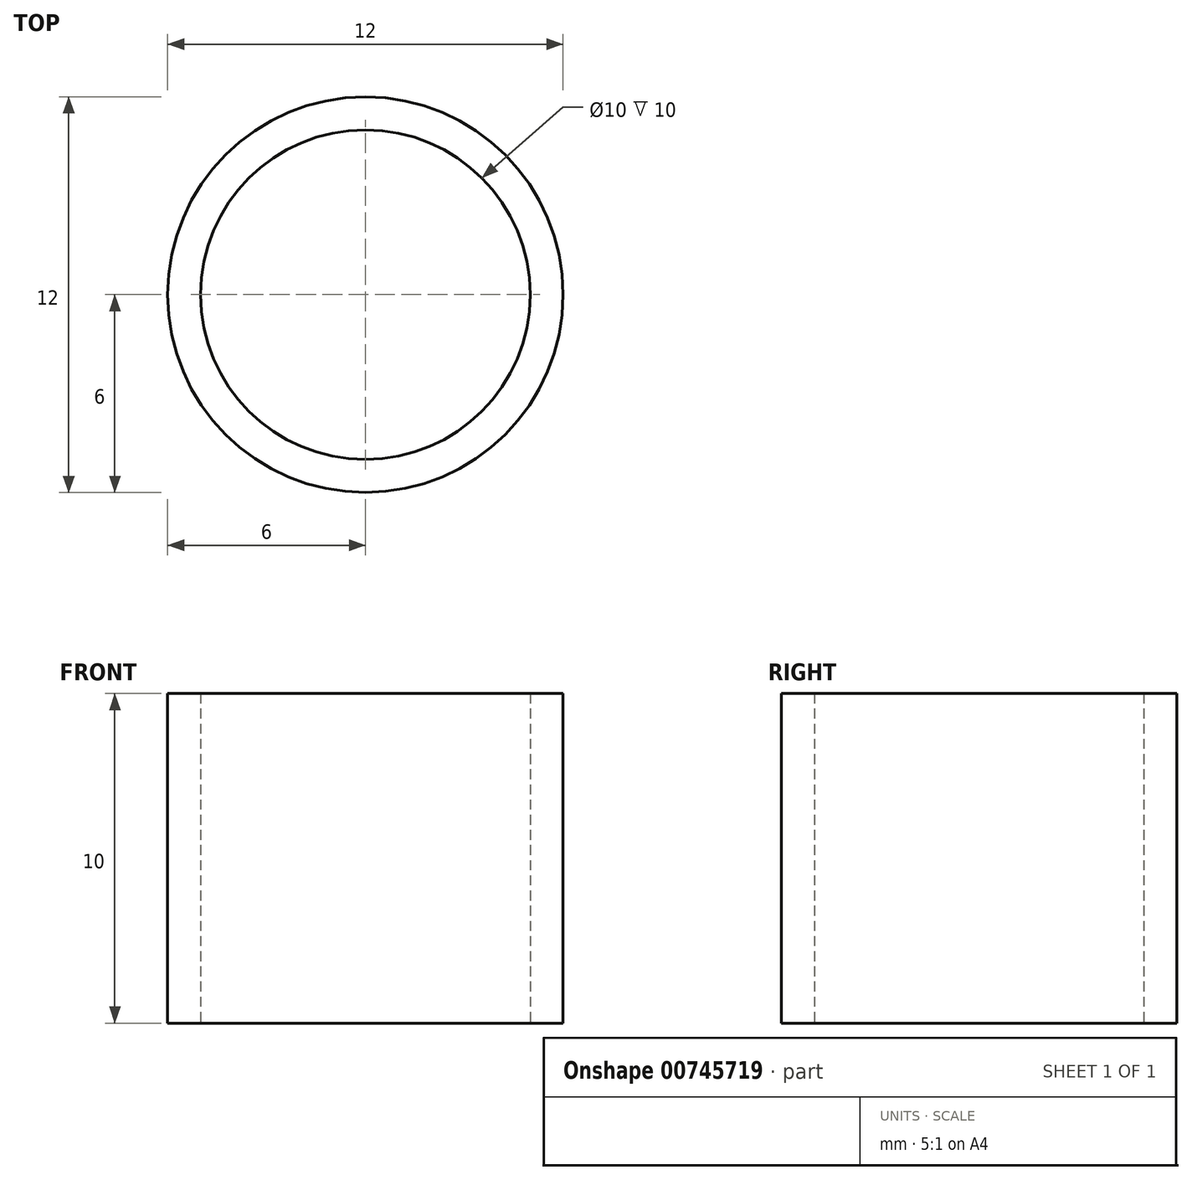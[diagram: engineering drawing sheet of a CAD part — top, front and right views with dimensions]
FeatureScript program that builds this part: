
annotation { "Feature Type Name" : "Feature", "Feature Type Description" : "" }
export const myFeature = defineFeature(function(context is Context, id is Id, definition is map)
    precondition{}
    {
        {
            var Q0;
            Q0=qCreatedBy(makeId("Top.planeOp"),FACE);
            var sketch = newSketch(context, id + "F0", { "sketchPlane" : qUnion([Q0])});
            skCircle(sketch, "E0", {"center": v(0, 0) * mm, "radius": 5 * mm});
            skCircle(sketch, "E1", {"center": v(0, 0) * mm, "radius": 6 * mm});
            skSolve(sketch);
        }
        {
            var Q0;
            Q0=makeQuery(id+"F0.imprint","IMPRINT",FACE,{"disambiguationData":[TD([[makeQuery(id+"F0.imprint","IMPRINT",EDGE,{"derivedFrom":sQuery(id+"F0.wireOp",EDGE,"E0")}),-1.0]])]});
            var Q1;
            Q1=sQuery(id+"F0.wireOp",EDGE,"E1");
            var Q2;
            Q2=sQuery(id+"F0.wireOp",EDGE,"E0");
            extrude(context, id + "F1", {"entities" : qUnion([Q0]), "surfaceEntities" : qUnion([Q1, Q2]), "depth" : 10 * mm, "offsetDistance" : 25 * mm});
        }
    });
